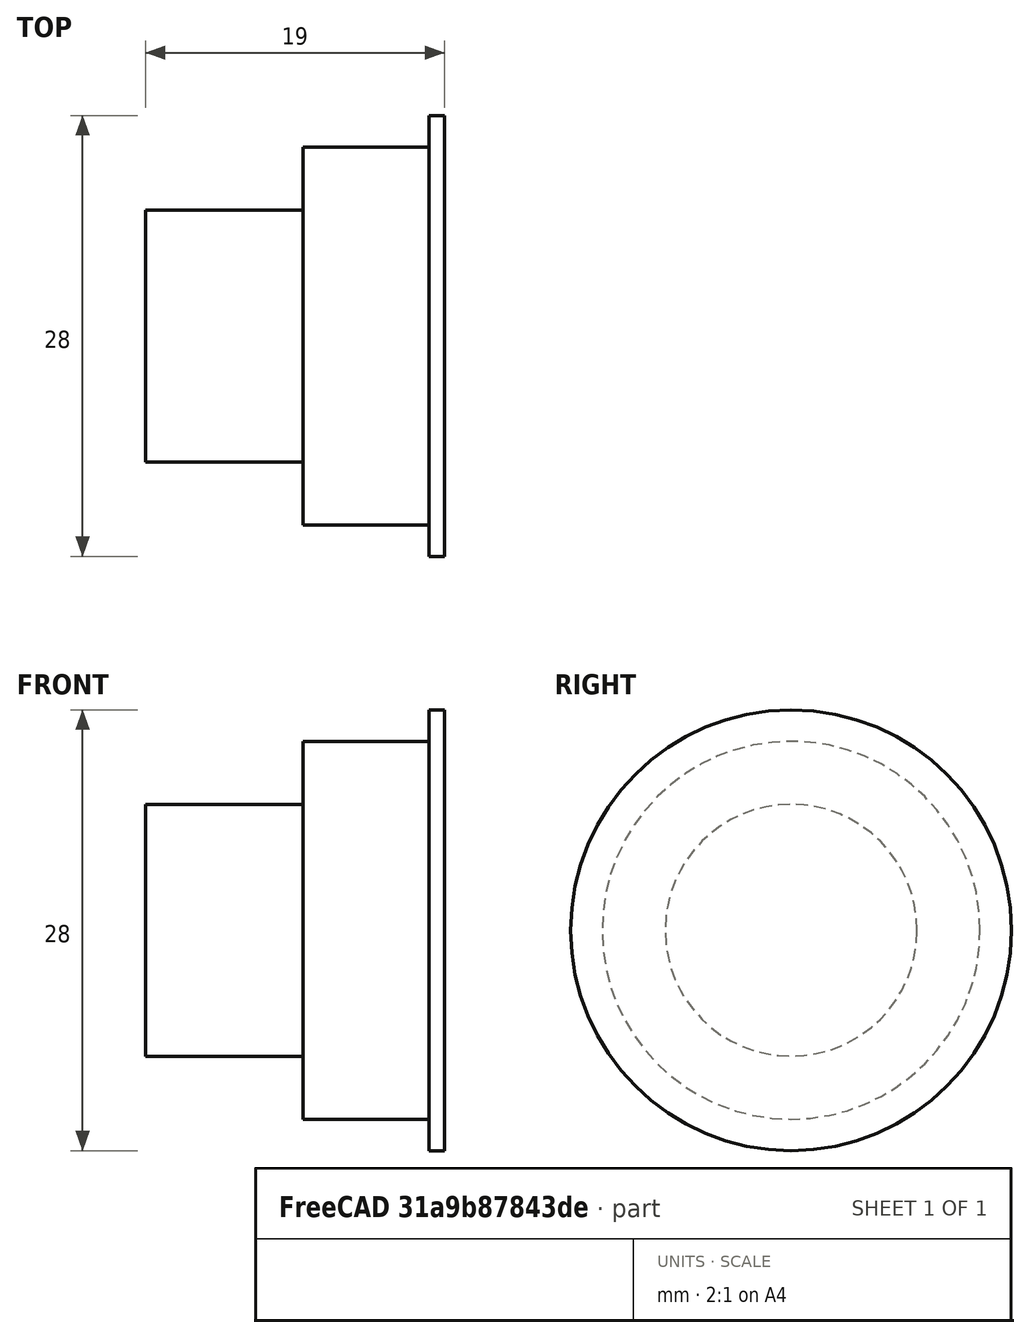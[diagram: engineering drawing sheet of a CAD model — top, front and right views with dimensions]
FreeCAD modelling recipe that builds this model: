
FCSTD DOCUMENT  (FreeCAD 1.0R39109 (Git))
Label: 04_Revolucao
License: All rights reserved
LicenseURL: https://en.wikipedia.org/wiki/All_rights_reserved
objects: Sketcher::SketchObject×1, PartDesign::Revolution×1, PartDesign::Body×1
note: 6 computed .brp shape members not serialized (recipe doc carries the construction recipe); baked Part::Feature solids carry a one-line shape summary decoded from their .brp

FEATURE [Sketcher::SketchObject] Sketch
  ArcFitTolerance = 1e-06
  AttachmentSupport = -> [XZ_Plane]
  FullyConstrained = true
  MakeInternals = false
  MapMode = 5
  Placement = pos=(0,0,0) rot=(1,0,0;1.5708rad)
  sketch-geometry (8):
    g0: LineSegment StartX=-19 StartY=0 StartZ=0 EndX=-19 EndY=8 EndZ=0
    g1: LineSegment StartX=-19 StartY=8 StartZ=0 EndX=-9 EndY=8 EndZ=0
    g2: LineSegment StartX=-9 StartY=8 StartZ=0 EndX=-9 EndY=12 EndZ=0
    g3: LineSegment StartX=-9 StartY=12 StartZ=0 EndX=-1 EndY=12 EndZ=0
    g4: LineSegment StartX=-1 StartY=12 StartZ=0 EndX=-1 EndY=14 EndZ=0
    g5: LineSegment StartX=-1 StartY=14 StartZ=0 EndX=0 EndY=14 EndZ=0
    g6: LineSegment StartX=0 StartY=14 StartZ=0 EndX=0 EndY=0 EndZ=0
    g7: LineSegment StartX=0 StartY=0 StartZ=0 EndX=-19 EndY=0 EndZ=0
  constraints (23):
    c: PointOnObject(g0,g-1)
    c: Vertical(g0)
    c: Coincident(g0,g1)
    c: Horizontal(g1)
    c: Coincident(g1,g2)
    c: Vertical(g2)
    c: Coincident(g2,g3)
    c: Horizontal(g3)
    c: Coincident(g3,g4)
    c: Vertical(g4)
    c: Coincident(g4,g5)
    c: Horizontal(g5)
    c: Coincident(g5,g6)
    c: Coincident(g6,g-1)
    c: Vertical(g6)
    c: Coincident(g6,g7)
    c: Coincident(g7,g0)
    c: DistanceY(g0,g0) = 8
    c: DistanceY(g2,g2) = 4
    c: DistanceY(g4,g4) = 2
    c: DistanceX(g1,g1) = 10
    c: DistanceX(g3,g3) = 8
    c: DistanceX(g5,g5) = 1
FEATURE [PartDesign::Revolution] Revolution
  Angle = 360
  Angle2 = 60
  Axis = (1,0,0)
  Base = (0,0,0)
  Placement = pos=(0,0,0) rot=(1,0,0;1.5708rad)
  Profile = -> Sketch
  ReferenceAxis = -> Sketch [H_Axis]
  Refine = true
  Suppressed = false
  Type = 0
FEATURE [PartDesign::Body] Body
  AllowCompound = false
  Group = -> [Sketch,Revolution]
  Origin = -> Origin
  Tip = -> Revolution
